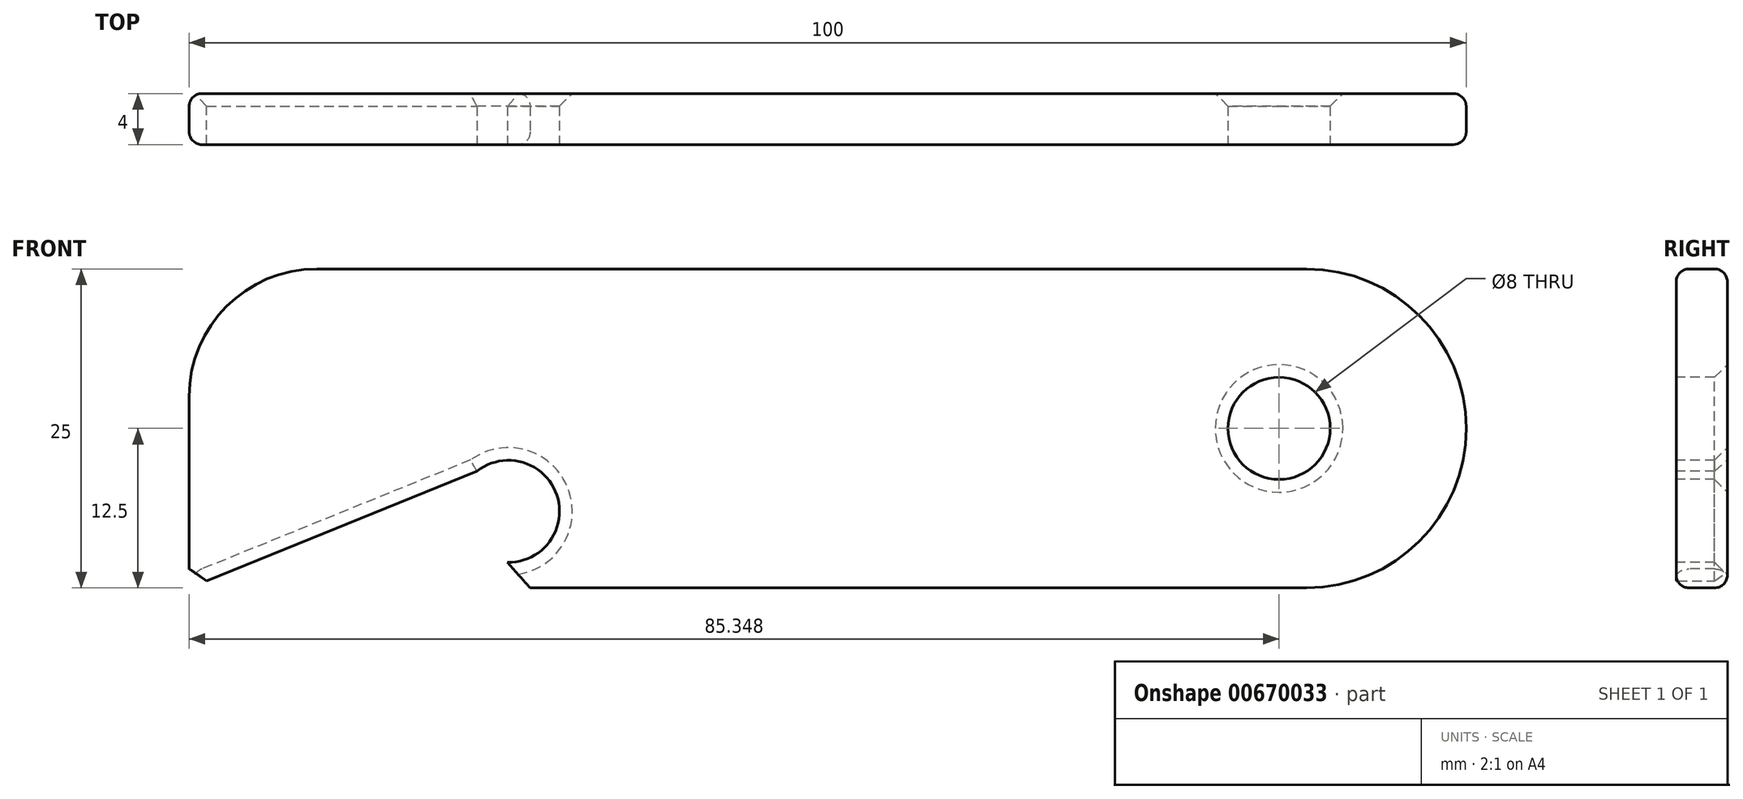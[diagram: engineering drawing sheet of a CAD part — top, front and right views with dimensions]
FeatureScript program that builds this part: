
annotation { "Feature Type Name" : "Feature", "Feature Type Description" : "" }
export const myFeature = defineFeature(function(context is Context, id is Id, definition is map)
    precondition{}
    {
        {
            var Q0;
            Q0=qCreatedBy(makeId("Front.planeOp"),FACE);
            var sketch = newSketch(context, id + "F0", { "sketchPlane" : qUnion([Q0])});
            skLineSegment(sketch, "E0.bottom", {"start": v(0, 0) * mm, "end": v(100, 0) * mm});
            skLineSegment(sketch, "E0.top", {"start": v(0, 25) * mm, "end": v(100, 25) * mm});
            skLineSegment(sketch, "E0.left", {"start": v(0, 0) * mm, "end": v(0, 25) * mm});
            skLineSegment(sketch, "E0.right", {"start": v(100, 0) * mm, "end": v(100, 25) * mm});
            skSolve(sketch);
        }
        {
            var Q0;
            Q0=makeQuery(id+"F0.imprint","IMPRINT",FACE,{"disambiguationData":[TD([[makeQuery(id+"F0.imprint","IMPRINT",EDGE,{"derivedFrom":sQuery(id+"F0.wireOp",EDGE,"E0.bottom")}),1.0]])]});
            extrude(context, id + "F1", {"entities" : qUnion([Q0]), "depth" : 4 * mm, "offsetDistance" : 25 * mm});
        }
        {
            var Q0;
            Q0=makeQuery(id+"F1.opExtrude","CAP_FACE",FACE,{"disambiguationData":[OSD([sQuery(id+"F0.wireOp",EDGE,"E0.bottom"),sQuery(id+"F0.wireOp",EDGE,"E0.top"),sQuery(id+"F0.wireOp",EDGE,"E0.left"),sQuery(id+"F0.wireOp",EDGE,"E0.right")])],"isStart":false});
            var sketch = newSketch(context, id + "F2", { "sketchPlane" : qUnion([Q0])});
            skCircle(sketch, "E1", {"center": v(85.35, 12.5) * mm, "radius": 4 * mm});
            skSolve(sketch);
        }
        {
            var Q0;
            Q0=makeQuery(id+"F2.imprint","IMPRINT",FACE,{"disambiguationData":[TD([[makeQuery(id+"F2.imprint","IMPRINT",EDGE,{"derivedFrom":sQuery(id+"F2.wireOp",EDGE,"E1")}),1.0]])]});
            extrude(context, id + "F3", {"entities" : qUnion([Q0]), "operationType" : NewBodyOperationType.REMOVE, "endBound" : BoundingType.THROUGH_ALL, "oppositeDirection" : true, "depth" : 25 * mm, "offsetDistance" : 25 * mm});
        }
        {
            var Q0;
            Q0=makeQuery(id+"F1.opExtrude","CAP_FACE",FACE,{"disambiguationData":[OSD([sQuery(id+"F0.wireOp",EDGE,"E0.bottom"),sQuery(id+"F0.wireOp",EDGE,"E0.top"),sQuery(id+"F0.wireOp",EDGE,"E0.left"),sQuery(id+"F0.wireOp",EDGE,"E0.right")])],"isStart":false});
            var sketch = newSketch(context, id + "F4", { "sketchPlane" : qUnion([Q0])});
            skCircle(sketch, "E2", {"center": v(25, 6) * mm, "radius": 4 * mm});
            skSolve(sketch);
        }
        {
            var Q0;
            Q0=makeQuery(id+"F1.opExtrude","SWEPT_EDGE",EDGE,{"disambiguationData":[OSD([sQuery(id+"F0.wireOp",EDGE,"E0.top"),sQuery(id+"F0.wireOp",EDGE,"E0.right")])]});
            var Q1;
            Q1=makeQuery(id+"F1.opExtrude","SWEPT_EDGE",EDGE,{"disambiguationData":[OSD([sQuery(id+"F0.wireOp",EDGE,"E0.bottom"),sQuery(id+"F0.wireOp",EDGE,"E0.right")])]});
            fillet(context, id + "F5", {"entities" : qUnion([Q0, Q1]), "radius" : 12.5 * mm, "tangentPropagation" : true, "allowEdgeOverflow" : false});
        }
        {
            var Q0;
            Q0=makeQuery(id+"F4.imprint","IMPRINT",FACE,{"disambiguationData":[TD([[makeQuery(id+"F4.imprint","IMPRINT",EDGE,{"derivedFrom":sQuery(id+"F4.wireOp",EDGE,"E2")}),1.0]])]});
            extrude(context, id + "F6", {"entities" : qUnion([Q0]), "operationType" : NewBodyOperationType.REMOVE, "endBound" : BoundingType.THROUGH_ALL, "oppositeDirection" : true, "depth" : 25 * mm, "offsetDistance" : 25 * mm});
        }
        {
            var Q0;
            Q0=makeQuery(id+"F1.opExtrude","CAP_FACE",FACE,{"disambiguationData":[OSD([sQuery(id+"F0.wireOp",EDGE,"E0.bottom"),sQuery(id+"F0.wireOp",EDGE,"E0.top"),sQuery(id+"F0.wireOp",EDGE,"E0.left"),sQuery(id+"F0.wireOp",EDGE,"E0.right")])],"isStart":false});
            var sketch = newSketch(context, id + "F7", { "sketchPlane" : qUnion([Q0])});
            skLineSegment(sketch, "E3", {"start": v(24.58, 9.98) * mm, "end": v(0, 0) * mm});
            skLineSegment(sketch, "E4", {"start": v(24.93, 2) * mm, "end": v(26.7, 0) * mm});
            skSolve(sketch);
        }
        {
            var Q0;
            {var subQ5=sQuery(id+"F7.wireOp",EDGE,"E4");Q0=makeQuery(id+"F7.imprint","IMPRINT",FACE,{"disambiguationData":[TD([[makeQuery(id+"F7.imprint","IMPRINT",EDGE,{"derivedFrom":subQ5}),-1.0]])]});}
            extrude(context, id + "F8", {"entities" : qUnion([Q0]), "operationType" : NewBodyOperationType.REMOVE, "endBound" : BoundingType.THROUGH_ALL, "oppositeDirection" : true, "depth" : 25 * mm, "offsetDistance" : 25 * mm});
        }
        {
            var Q0;
            Q0=makeQuery(id+"F1.opExtrude","SWEPT_EDGE",EDGE,{"disambiguationData":[OSD([sQuery(id+"F0.wireOp",EDGE,"E0.top"),sQuery(id+"F0.wireOp",EDGE,"E0.left")])]});
            fillet(context, id + "F9", {"entities" : qUnion([Q0]), "radius" : 10 * mm, "tangentPropagation" : true, "allowEdgeOverflow" : false});
        }
        {
            var Q0;
            Q0=makeQuery(id+"F3.boolean.opBoolean","COPY",EDGE,{"derivedFrom":makeQuery(id+"F3.opExtrude","CAP_EDGE",EDGE,{"disambiguationData":[OSD([sQuery(id+"F2.wireOp",EDGE,"E1")])],"isStart":true})});
            var Q1;
            Q1=makeQuery(id+"F6.boolean.opBoolean","COPY",EDGE,{"derivedFrom":makeQuery(id+"F6.opExtrude","CAP_EDGE",EDGE,{"disambiguationData":[OSD([sQuery(id+"F4.wireOp",EDGE,"E2")])],"isStart":true})});
            var Q2;
            Q2=makeQuery(id+"F6.boolean.opBoolean","INTERSECT",EDGE,{"derivedFrom":[makeQuery(id+"F1.opExtrude","CAP_FACE",FACE,{"disambiguationData":[OSD([sQuery(id+"F0.wireOp",EDGE,"E0.bottom"),sQuery(id+"F0.wireOp",EDGE,"E0.top"),sQuery(id+"F0.wireOp",EDGE,"E0.left"),sQuery(id+"F0.wireOp",EDGE,"E0.right")])],"isStart":true}),makeQuery(id+"F6.opExtrude","SWEPT_FACE",FACE,{"disambiguationData":[OSD([sQuery(id+"F4.wireOp",EDGE,"E2")])]})]});
            var Q3;
            Q3=makeQuery(id+"F3.boolean.opBoolean","INTERSECT",EDGE,{"derivedFrom":[makeQuery(id+"F1.opExtrude","CAP_FACE",FACE,{"disambiguationData":[OSD([sQuery(id+"F0.wireOp",EDGE,"E0.bottom"),sQuery(id+"F0.wireOp",EDGE,"E0.top"),sQuery(id+"F0.wireOp",EDGE,"E0.left"),sQuery(id+"F0.wireOp",EDGE,"E0.right")])],"isStart":true}),makeQuery(id+"F3.opExtrude","SWEPT_FACE",FACE,{"disambiguationData":[OSD([sQuery(id+"F2.wireOp",EDGE,"E1")])]})]});
            chamfer(context, id + "F10", {"entities" : qUnion([Q0, Q1, Q2, Q3]), "width" : (1) * mm, "tangentPropagation" : true});
        }
        {
            var Q0;
            Q0=makeQuery(id+"F8.boolean.opBoolean","COPY",EDGE,{"derivedFrom":makeQuery(id+"F8.opExtrude","CAP_EDGE",EDGE,{"disambiguationData":[OSD([sQuery(id+"F7.wireOp",EDGE,"E3")])],"isStart":true})});
            var Q1;
            Q1=makeQuery(id+"F8.boolean.opBoolean","INTERSECT",EDGE,{"derivedFrom":[makeQuery(id+"F1.opExtrude","CAP_FACE",FACE,{"disambiguationData":[OSD([sQuery(id+"F0.wireOp",EDGE,"E0.bottom"),sQuery(id+"F0.wireOp",EDGE,"E0.top"),sQuery(id+"F0.wireOp",EDGE,"E0.left"),sQuery(id+"F0.wireOp",EDGE,"E0.right")])],"isStart":true}),makeQuery(id+"F8.opExtrude","SWEPT_FACE",FACE,{"disambiguationData":[OSD([sQuery(id+"F7.wireOp",EDGE,"E3")])]})]});
            var Q2;
            {var subQ0=sQuery(id+"F0.wireOp",EDGE,"E0.left");var subQ1=sQuery(id+"F0.wireOp",EDGE,"E0.bottom");Q2=makeQuery(id+"F8.boolean.opBoolean","MERGE",EDGE,{"derivedFrom":[makeQuery(id+"F1.opExtrude","SWEPT_EDGE",EDGE,{"disambiguationData":[OSD([subQ1,subQ0])]}),makeQuery(id+"F8.opExtrude","SWEPT_EDGE",EDGE,{"disambiguationData":[OSD([subQ1,subQ0,sQuery(id+"F7.wireOp",EDGE,"E3")])]})]});}
            chamfer(context, id + "F11", {"entities" : qUnion([Q0, Q1, Q2]), "width" : 1 * mm, "tangentPropagation" : true});
        }
        {
            var Q0;
            Q0=makeQuery(id+"F1.opExtrude","CAP_EDGE",EDGE,{"disambiguationData":[OSD([sQuery(id+"F0.wireOp",EDGE,"E0.bottom")])],"isStart":false});
            var Q1;
            Q1=makeQuery(id+"F1.opExtrude","CAP_EDGE",EDGE,{"disambiguationData":[OSD([sQuery(id+"F0.wireOp",EDGE,"E0.bottom")])],"isStart":true});
            fillet(context, id + "F12", {"entities" : qUnion([Q0, Q1]), "radius" : 1 * mm, "tangentPropagation" : true, "allowEdgeOverflow" : false});
        }
    });
